# Revit family: Plumbing Fixture-Grease_Interseptor_Mifab_MI-G-L
name_source: partatom
category: Plumbing Fixtures
revit_build: Autodesk Revit Structure 2013 (Build: 20120221_2030(x64)
units: mm (PartAtom-declared; Revit-internal decimal feet)

## types (3) — shared parameters
C = 4 "
D = 7 "
Description = Low Rough In P.D.I Certified 4 to 50 GPM Grease Interceptor
E = 11 "
F = 3 "
Interceptor Material = Acid Resistant Epoxy Coated Green
Manufacturer = MIFAB
Standard Inlet And Outlet Radii = 1.5 "
URL = www.mifab.com
zero-valued in all types: Default Elevation, WFU

## per-type parameters (varying)
| type | A | B | Flow Rate | Grease Capacity | Water Capacity |
| MI-G-L-20 | 34 " | 24 " | 20 GPM | 40 lbs | 16.76 Gallons |
| MI-G-L-35 | 42 " | 28 " | 35 GPM | 70 lbs | 24.76 Gallons |
| MI-G-L-50 | 46 " | 30 " | 50 GPM | 100 lbs | 29.33 Gallons |

note: column(s) folded — value = type name in every type: Model

## geometry (parser evidence)
native form markers: Blend x7, Sweep x1
no freeform markers — native parametric forms only
